# Revit family: Gleitlager T ohne Schalldämmung, Ø20 bis Ø60mm
name_source: partatom
category: HLS-Bauteile
revit_build: Autodesk Revit 2018 (Build: 20190510_1515(x64)
units: mm (PartAtom-declared; Revit-internal decimal feet)

## family parameters
Arbeitsebenenbasiert = Ja
Beim Laden mit Abzugskörper schneiden = Nein
Bemaßung runder Anschluss = Durchmesser verwenden
Gemeinsam genutzt = Ja
Immer vertikal = Nein
Klassifizierung = Keine
Raumberechnungspunkt = Nein
Teiletyp = Normal

## types (9) — shared parameters
Breite Schellenband = 35 mm
Breite Unterbau = 100 mm
Fabrikat = MEFA
Hersteller = MEFA
Höhe Unterbau = 104 mm
Kurztext1 = Gleitlager T h=104 35 x 4 mm
Länge Unterbau = 250 mm
Mengeneinheit = St
Schalldämmeinlage = ohne Dämmung
Sicherheitsfaktor = 1.54
Verschluss-Schraube = M10
Vorgabe-Ansicht = 1219 mm
vpe = 1
zero-valued in all types: Dämmstärke, Stärke

## per-type parameters (varying)
| type | Artikelnummer | EAN | Gewicht | Gewicht pro Bauteil | Kurztext2 | RS Titan 35x4 | max. Rohraußendurchmesser | min. Rohraußendurchmesser |
| Gleitlager T Ø  60, o.Däm. | 145fa0060 | 4250928459893 | 5.36 kg | 5.36 kg | 60 mm o. Dämm. fsv | Rohrschelle Titan HD, o.A, o.D, Ø22 bis 60mm, 30Grad : Titan HD, o.A., Ø60mm | 0 mm  [stored 0 ft] | 0 mm  [stored 0 ft] |
| Gleitlager T Ø  54, o.Däm. | 145fa0054 | 4250928459886 | 5.29 kg | 5.29 kg | 54 mm o. Dämm. fsv | Rohrschelle Titan HD, o.A, o.D, Ø22 bis 60mm, 30Grad : Titan HD, o.A., Ø54mm | 0 mm  [stored 0 ft] | 0 mm  [stored 0 ft] |
| Gleitlager T Ø  48-50, o.Däm. | 145fa0050 | 4250928459879 | 5.26 kg | 5.26 kg | 48 - 50 mm o. Dämm. fsv | Rohrschelle Titan HD, o.A, o.D, Ø22 bis 60mm, 30Grad : Titan HD, o.A., Ø49mm | 50 mm  [stored 0.164042 ft] | 48 mm  [stored 0.15748 ft] |
| Gleitlager T Ø  40-42, o.Däm. | 145fa0042 | 4250928459862 | 5.20 kg | 5.20 kg | 40 - 42 mm o. Dämm. fsv | Rohrschelle Titan HD, o.A, o.D, Ø22 bis 60mm, 30Grad : Titan HD, o.A., Ø42mm | 42 mm  [stored 0.137795 ft] | 40 mm  [stored 0.131234 ft] |
| Gleitlager T Ø  33-35, o.Däm. | 145fa0035 | 4250928459855 | 5.14 kg | 5.14 kg | 33 - 35 mm o. Dämm. fsv | Rohrschelle Titan HD, o.A, o.D, Ø22 bis 60mm, 30Grad : Titan HD, o.A., Ø35mm | 35 mm  [stored 0.114829 ft] | 33 mm  [stored 0.108268 ft] |
| Gleitlager T Ø  32, o.Däm. | 145fa0032 | 4250928459848 | 5.12 kg | 5.12 kg | 32 mm o. Dämm. fsv | Rohrschelle Titan HD, o.A, o.D, Ø22 bis 60mm, 30Grad : Titan HD, o.A., Ø32mm | 0 mm  [stored 0 ft] | 0 mm  [stored 0 ft] |
| Gleitlager T Ø  27-28, o.Däm. | 145fa0028 | 4250928459831 | 5.09 kg | 5.09 kg | 27 - 28 mm o. Dämm. fsv | Rohrschelle Titan HD, o.A, o.D, Ø22 bis 60mm, 30Grad : Titan HD, o.A., Ø28mm | 28 mm  [stored 0.0918635 ft] | 27 mm  [stored 0.0885827 ft] |
| Gleitlager T Ø  25, o.Däm. | 145fa0025 | 4250928459824 | 5.05 kg | 5.05 kg | 25 mm o. Dämm. fsv | Rohrschelle Titan HD, o.A, o.D, Ø22 bis 60mm, 30Grad : Titan HD, o.A., Ø25mm | 0 mm  [stored 0 ft] | 0 mm  [stored 0 ft] |
| Gleitlager T Ø  20-22, o.Däm. | 145fa0022 | 4250928459817 | 5.03 kg | 5.03 kg | 20 - 22 mm o. Dämm. fsv | Rohrschelle Titan HD, o.A, o.D, Ø22 bis 60mm, 30Grad : Titan HD, o.A., Ø22mm | 22 mm  [stored 0.0721785 ft] | 20 mm  [stored 0.0656168 ft] |

note: [stored X ft] marks values corroborated as IEEE doubles in the binary element streams (Revit-internal decimal feet)

## geometry (parser evidence)
native form markers: Sweep x3
no freeform markers — native parametric forms only
